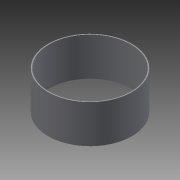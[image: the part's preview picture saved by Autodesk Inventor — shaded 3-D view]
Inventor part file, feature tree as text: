
AUTODESK INVENTOR PART (.ipt)
format: ipt  version: 2015 (Build 190159000, 159)  size: 87,552 bytes
history: native  units: in
note: dims shown in document units (in); Inventor stores cm internally (conversion verified against a paired STEP export)
features: extrude x1, sketch x1
ambient origin geometry x8: Origin, YZ Plane, XZ Plane, XY Plane, X Axis, Y Axis, Z Axis, Center Point
bodies: Body1 (feature_tree)
feature tree (2):
  extrude  "Extrusion2"  Depth=3.5in
  sketch  "Sketch1"  dims[d0=7.5in d1=0.0945in d4=3.5in d5=0.0in]
